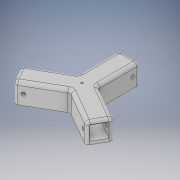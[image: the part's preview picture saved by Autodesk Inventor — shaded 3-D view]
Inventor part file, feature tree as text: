
AUTODESK INVENTOR PART (.ipt)
format: ipt  version: 2019.4 (Build 234330000, 330)  size: 222,720 bytes
history: native  units: mm
features: extrude x4, sketch x4, pattern_circular x3, fillet x3
ambient origin geometry x8: Origin, YZ Plane, XZ Plane, XY Plane, X Axis, Y Axis, Z Axis, Center Point
bodies: Solid1 (feature_tree)
feature tree (14):
  extrude  "Extrusion1"  Depth=70.0mm
  extrude  "Extrusion6"  Depth=30.0mm
  pattern_circular  "Circular Pattern4"  Count=3  [1 undecoded]
  extrude  "Extrusion7"  Depth=21.0mm
  pattern_circular  "Circular Pattern5"  [2 undecoded]
  extrude  "Extrusion8"  Depth=30.0mm TaperAngle=360.0deg
  pattern_circular  "Circular Pattern6"  [2 undecoded]
  fillet  "Fillet5"  Radius=5.5mm
  fillet  "Fillet6"  Radius=30.0mm
  fillet  "Fillet7"  Radius=30.0mm
  sketch  "Sketch1"  dims[d0=30.0mm d1=70.0mm]
  sketch  "Sketch6"  dims[d2=30.0mm d3=0.0mm d32=3.0mm d33=30.0mm d34=0.0mm]
  sketch  "Sketch7"  dims[d35=30.0mm d36=360.0deg d38=21.0mm]
  sketch  "Sketch8"  dims[d39=21.0mm d40=45.0mm d41=0.0mm d42=30.0mm d43=360.0deg d45=10.0mm d46=5.5mm d47=30.0mm d48=0.0mm d49=30.0mm d50=360.0deg d52=5.0mm d53=5.0mm d54=4.0mm]
note: 5 required parameter values undecoded (feature->parameter linkage not recoverable at this tier; creation-order binding heuristic only, values carry confidence <= 0.55)
